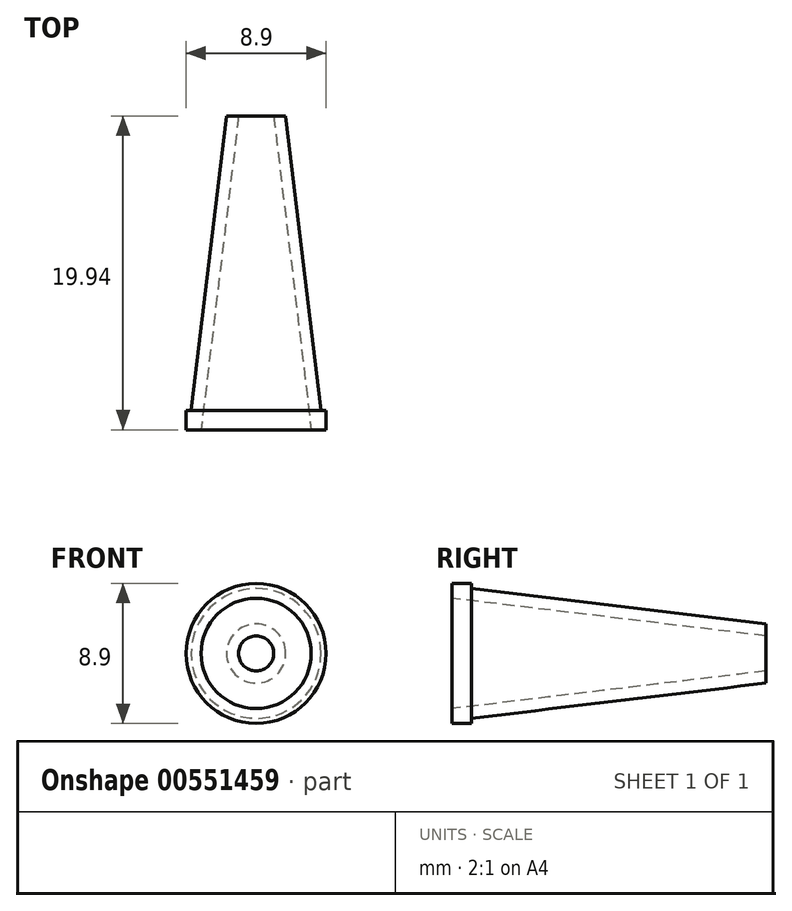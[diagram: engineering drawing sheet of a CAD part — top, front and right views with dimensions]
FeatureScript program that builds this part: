
annotation { "Feature Type Name" : "Feature", "Feature Type Description" : "" }
export const myFeature = defineFeature(function(context is Context, id is Id, definition is map)
    precondition{}
    {
        {
            var Q0;
            Q0=qCreatedBy(makeId("Front.planeOp"),FACE);
            var sketch = newSketch(context, id + "F0", { "sketchPlane" : qUnion([Q0])});
            skCircle(sketch, "E0", {"center": v(0, 0) * mm, "radius": 4.27 * mm});
            skSolve(sketch);
        }
        {
            var Q0;
            Q0=qCreatedBy(makeId("Front.planeOp"),FACE);
            cPlane(context, id + "F1", {"entities" : qUnion([Q0]), "cplaneType" : CPlaneType.OFFSET, "offset" : 19.94 * mm, "oppositeDirection" : true, "width" : 152.4 * mm, "height" : 152.4 * mm});
        }
        {
            var Q0;
            Q0=qCreatedBy(id+"F1.planeOp",FACE);
            var sketch = newSketch(context, id + "F2", { "sketchPlane" : qUnion([Q0])});
            skCircle(sketch, "E1", {"center": v(0, 0) * mm, "radius": 1.88 * mm});
            skSolve(sketch);
        }
        {
            var Q0;
            Q0 = qSketchRegion(id + "F0", true);
            var Q1;
            Q1 = qSketchRegion(id + "F2", true);
            loft(context, id + "F3", {"sheetProfilesArray" : [{ "sheetProfileEntities" : qUnion([Q0]) }, { "sheetProfileEntities" : qUnion([Q1]) }]});
        }
        {
            var Q0;
            Q0=makeQuery(id+"F3.opLoft","CAP_FACE",FACE,{"disambiguationData":[OSD([makeQuery(id+"F0.imprint","IMPRINT",FACE,{"disambiguationData":[TD([[makeQuery(id+"F0.imprint","IMPRINT",EDGE,{"derivedFrom":sQuery(id+"F0.wireOp",EDGE,"E0")}),1.0]])]})])],"isStart":true});
            var Q1;
            Q1=makeQuery(id+"F3.opLoft","CAP_FACE",FACE,{"disambiguationData":[OSD([makeQuery(id+"F2.imprint","IMPRINT",FACE,{"disambiguationData":[TD([[makeQuery(id+"F2.imprint","IMPRINT",EDGE,{"derivedFrom":sQuery(id+"F2.wireOp",EDGE,"E1")}),1.0]])]})])],"isStart":true});
            var Q2;
            Q2=makeQuery(id+"F3.opLoft","SWEPT_BODY",BODY,{"disambiguationData":[OSD([makeQuery(id+"F0.imprint","IMPRINT",FACE,{"disambiguationData":[TD([[makeQuery(id+"F0.imprint","IMPRINT",EDGE,{"derivedFrom":sQuery(id+"F0.wireOp",EDGE,"E0")}),1.0]])]}),makeQuery(id+"F2.imprint","IMPRINT",FACE,{"disambiguationData":[TD([[makeQuery(id+"F2.imprint","IMPRINT",EDGE,{"derivedFrom":sQuery(id+"F2.wireOp",EDGE,"E1")}),1.0]])]})])]});
            shell(context, id + "F4", {"entities" : qUnion([Q0, Q1]), "parts" : qUnion([Q2]), "thickness" : 0.76 * mm});
        }
        {
            var Q0;
            Q0=qCreatedBy(makeId("Front.planeOp"),FACE);
            var sketch = newSketch(context, id + "F5", { "sketchPlane" : qUnion([Q0])});
            skCircle(sketch, "E2", {"center": v(0, 0) * mm, "radius": 4.45 * mm});
            skCircle(sketch, "E3.0", {"center": v(0, 0) * mm, "radius": 3.5 * mm});
            skSolve(sketch);
        }
        {
            var Q0;
            Q0=makeQuery(id+"F5.imprint","IMPRINT",FACE,{"disambiguationData":[TD([[makeQuery(id+"F5.imprint","IMPRINT",EDGE,{"derivedFrom":sQuery(id+"F5.wireOp",EDGE,"E2")}),1.0]])]});
            extrude(context, id + "F6", {"entities" : qUnion([Q0]), "operationType" : NewBodyOperationType.ADD, "oppositeDirection" : true, "depth" : 1.22 * mm, "offsetDistance" : 25.4 * mm});
        }
    });
